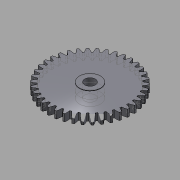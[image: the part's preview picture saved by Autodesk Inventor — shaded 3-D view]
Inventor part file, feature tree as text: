
AUTODESK INVENTOR PART (.ipt)
format: ipt  version: 2015 (Build 190159000, 159)  size: 347,136 bytes
history: native  units: in
note: dims shown in document units (in); Inventor stores cm internally (conversion verified against a paired STEP export)
features: other x13, sketch x5, plane x2
ambient origin geometry x8: Origin, YZ Plane, XZ Plane, XY Plane, X Axis, Y Axis, Z Axis, Center Point
bodies: Solid1 (feature_tree)
feature tree (20):
  other  "Spur Gear28_MIR2.ipt"
  other  "Solid1::Spur Gear28_MIR2.ipt"
  other  "TaggingFeature1"
  sketch  "Sketch1"  dims[d0=0.3937in]
  sketch  "Sketch2"  dims[d16=0.5709in d17=0.0in d41=0.0in d43=0.5709in d46=0.5709in d47=0.0in d48=0.0in]
  sketch  "Sketch3"
  sketch  "Sketch4"
  sketch  "Sketch5"
  plane  "XZ Plane_1"
  plane  "Work Plane2"
  other  "Z Axis_1"
  other  "Srf1"
  other  "Srf1::Derived"
  other  "Distance iMate"
  other  "Align iMate"
  other  "Mesh iMate"
  other  "Axis iMate"
  other  "Position iMate"
  other  "Mesh iMate2"
  other  "Start plane iMate"
